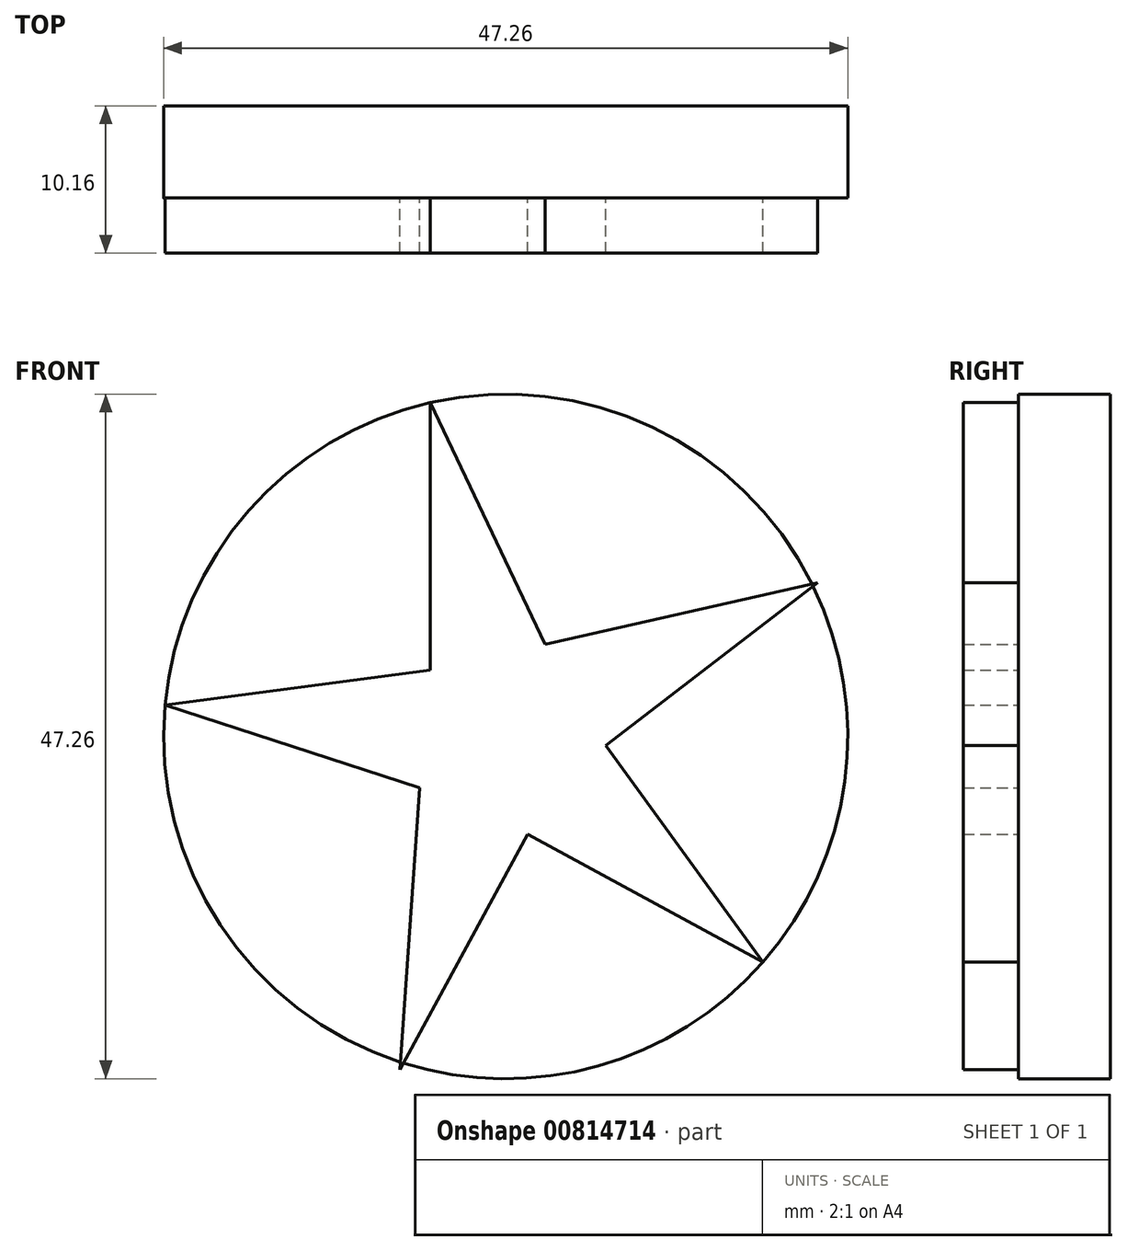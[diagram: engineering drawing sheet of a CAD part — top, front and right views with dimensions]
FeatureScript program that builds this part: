
annotation { "Feature Type Name" : "Feature", "Feature Type Description" : "" }
export const myFeature = defineFeature(function(context is Context, id is Id, definition is map)
    precondition{}
    {
        {
            var Q0;
            Q0=qCreatedBy(makeId("Front.planeOp"),FACE);
            var sketch = newSketch(context, id + "F0", { "sketchPlane" : qUnion([Q0])});
            skCircle(sketch, "E0", {"center": v(0, 0) * mm, "radius": 23.63 * mm});
            skSolve(sketch);
        }
        {
            var Q0;
            Q0 = qSketchRegion(id + "F0", true);
            extrude(context, id + "F1", {"entities" : qUnion([Q0]), "depth" : 6.35 * mm, "offsetDistance" : 25.4 * mm});
        }
        {
            var Q0;
            Q0=makeQuery(id+"F1.opExtrude","CAP_FACE",FACE,{"disambiguationData":[OSD([sQuery(id+"F0.wireOp",EDGE,"E0")])],"isStart":false});
            var sketch = newSketch(context, id + "F2", { "sketchPlane" : qUnion([Q0])});
            skCircle(sketch, "E1.cCircle", {"center": v(0, 0) * mm, "radius": 5.6 * mm, "construction": true});
            skLineSegment(sketch, "E1.0", {"start": v(6.9, -0.64) * mm, "end": v(1.53, -6.76) * mm});
            skLineSegment(sketch, "E1.1", {"start": v(1.53, -6.76) * mm, "end": v(-5.96, -3.54) * mm});
            skLineSegment(sketch, "E1.2", {"start": v(-5.96, -3.54) * mm, "end": v(-5.21, 4.57) * mm});
            skLineSegment(sketch, "E1.3", {"start": v(-5.21, 4.57) * mm, "end": v(2.74, 6.37) * mm});
            skLineSegment(sketch, "E1.4", {"start": v(2.74, 6.37) * mm, "end": v(6.9, -0.64) * mm});
            skPoint(sketch, "E1.0.midPoint", {"position": v(4.22, -3.7) * mm});
            skLineSegment(sketch, "E2", {"start": v(-5.21, 4.57) * mm, "end": v(-5.21, 23.05) * mm});
            skLineSegment(sketch, "E3", {"start": v(2.74, 6.37) * mm, "end": v(-5.21, 23.05) * mm});
            skLineSegment(sketch, "E4", {"start": v(2.74, 6.37) * mm, "end": v(21.56, 10.62) * mm});
            skLineSegment(sketch, "E5", {"start": v(6.9, -0.64) * mm, "end": v(17.77, -15.59) * mm});
            skLineSegment(sketch, "E6", {"start": v(1.53, -6.76) * mm, "end": v(17.77, -15.59) * mm});
            skLineSegment(sketch, "E7", {"start": v(1.53, -6.76) * mm, "end": v(-7.3, -23) * mm});
            skLineSegment(sketch, "E8", {"start": v(-5.96, -3.54) * mm, "end": v(-23.54, 2.17) * mm});
            skLineSegment(sketch, "E9", {"start": v(-23.54, 2.17) * mm, "end": v(-5.21, 4.57) * mm});
            skLineSegment(sketch, "E10", {"start": v(21.56, 10.62) * mm, "end": v(6.9, -0.64) * mm});
            skLineSegment(sketch, "E11", {"start": v(-7.3, -23) * mm, "end": v(-5.96, -3.54) * mm});
            skSolve(sketch);
        }
        {
            var Q0;
            Q0 = qSketchRegion(id + "F2", true);
            extrude(context, id + "F3", {"entities" : qUnion([Q0]), "operationType" : NewBodyOperationType.ADD, "depth" : 3.8 * mm, "offsetDistance" : 25.4 * mm});
        }
    });
